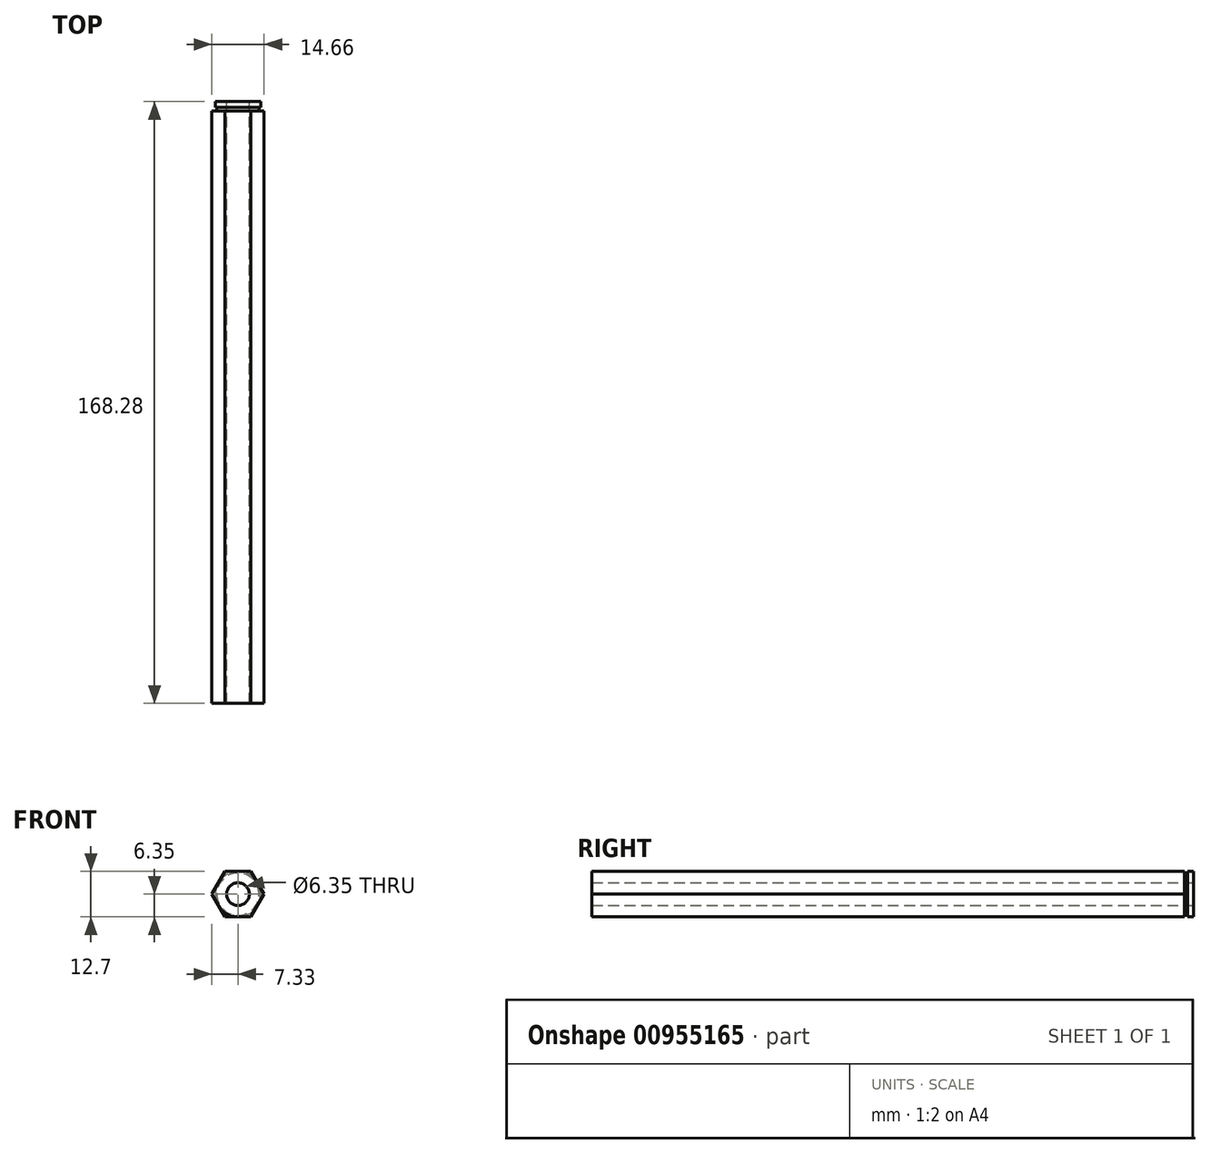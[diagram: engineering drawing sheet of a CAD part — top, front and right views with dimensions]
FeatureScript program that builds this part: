
annotation { "Feature Type Name" : "Feature", "Feature Type Description" : "" }
export const myFeature = defineFeature(function(context is Context, id is Id, definition is map)
    precondition{}
    {
        {
            var Q0;
            Q0=qCreatedBy(makeId("Front.planeOp"),FACE);
            var sketch = newSketch(context, id + "F0", { "sketchPlane" : qUnion([Q0])});
            skCircle(sketch, "E0.cCircle", {"center": v(0, 0) * mm, "radius": 6.35 * mm, "construction": true});
            skLineSegment(sketch, "E0.0", {"start": v(-3.67, 6.35) * mm, "end": v(3.67, 6.35) * mm});
            skLineSegment(sketch, "E0.1", {"start": v(3.67, 6.35) * mm, "end": v(7.33, 0) * mm});
            skLineSegment(sketch, "E0.2", {"start": v(7.33, 0) * mm, "end": v(3.67, -6.35) * mm});
            skLineSegment(sketch, "E0.3", {"start": v(3.67, -6.35) * mm, "end": v(-3.67, -6.35) * mm});
            skLineSegment(sketch, "E0.4", {"start": v(-3.67, -6.35) * mm, "end": v(-7.33, 0) * mm});
            skLineSegment(sketch, "E0.5", {"start": v(-7.33, 0) * mm, "end": v(-3.67, 6.35) * mm});
            skPoint(sketch, "E0.0.midPoint", {"position": v(0, 6.35) * mm});
            skCircle(sketch, "E1", {"center": v(0, 0) * mm, "radius": 3.18 * mm});
            skSolve(sketch);
        }
        {
            var Q0;
            Q0=qSketchRegion(id+"F0",true);
            extrude(context, id + "F1", {"entities" : qUnion([Q0]), "depth" : 168.27 * mm, "offsetDistance" : 25.4 * mm});
        }
        {
            var Q0;
            Q0=qCreatedBy(makeId("Top.planeOp"),FACE);
            var sketch = newSketch(context, id + "F2", { "sketchPlane" : qUnion([Q0])});
            skLineSegment(sketch, "E2", {"start": v(-6.35, 0) * mm, "end": v(-6.35, -1.59) * mm});
            skLineSegment(sketch, "E3", {"start": v(-6.35, -1.59) * mm, "end": v(-5.94, -1.59) * mm});
            skLineSegment(sketch, "E4", {"start": v(-5.94, -1.59) * mm, "end": v(-5.94, -2.58) * mm});
            skLineSegment(sketch, "E5", {"start": v(-5.94, -2.58) * mm, "end": v(-7.33, -2.58) * mm});
            skLineSegment(sketch, "E6", {"start": v(-7.33, -2.58) * mm, "end": v(-7.33, 0) * mm});
            skLineSegment(sketch, "E7", {"start": v(-7.33, 0) * mm, "end": v(-6.35, 0) * mm});
            skLineSegment(sketch, "E8", {"start": v(0, 0) * mm, "end": v(0, -2.58) * mm, "construction": true});
            skSolve(sketch);
        }
        {
            var Q0;
            Q0=qSketchRegion(id+"F2",true);
            var Q1;
            Q1=sQuery(id+"F2.wireOp",EDGE,"E8");
            revolve(context, id + "F3", {"operationType" : NewBodyOperationType.REMOVE, "surfaceOperationType" : NewSurfaceOperationType.NEW, "entities" : qUnion([Q0]), "axis" : qUnion([Q1]), "revolveType" : RevolveType.FULL, "oppositeDirection" : true});
        }
    });
